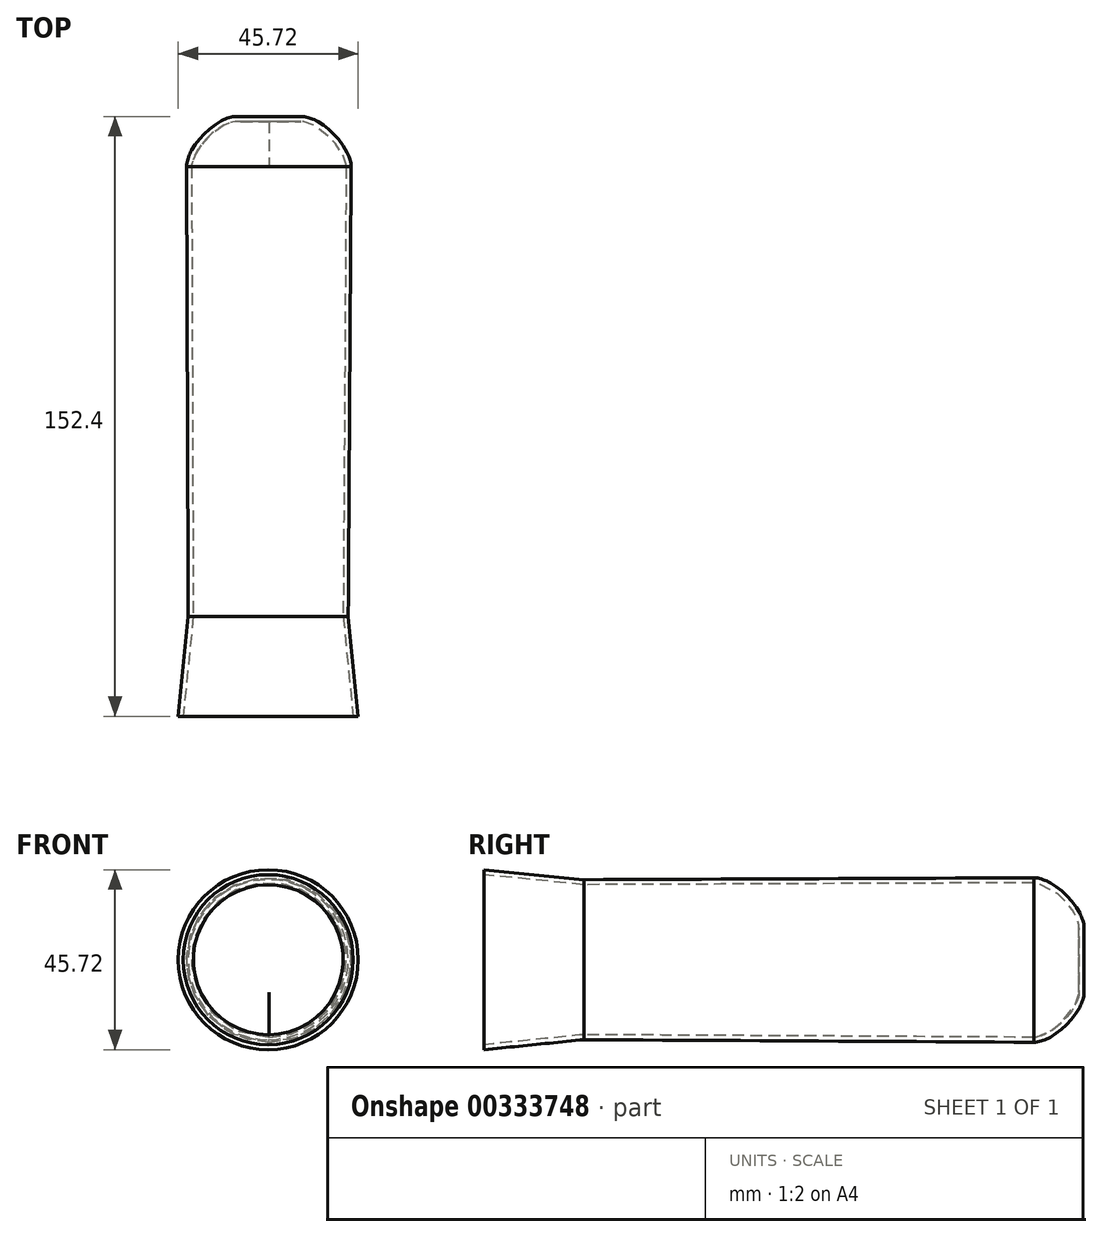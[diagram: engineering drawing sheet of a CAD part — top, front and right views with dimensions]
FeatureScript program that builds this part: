
annotation { "Feature Type Name" : "Feature", "Feature Type Description" : "" }
export const myFeature = defineFeature(function(context is Context, id is Id, definition is map)
    precondition{}
    {
        {
            var Q0;
            Q0=qCreatedBy(makeId("Front.planeOp"),FACE);
            var sketch = newSketch(context, id + "F0", { "sketchPlane" : qUnion([Q0])});
            skCircle(sketch, "E0", {"center": v(0, 0) * mm, "radius": 22.86 * mm});
            skSolve(sketch);
        }
        {
            var Q0;
            Q0=qCreatedBy(makeId("Front.planeOp"),FACE);
            cPlane(context, id + "F1", {"entities" : qUnion([Q0]), "cplaneType" : CPlaneType.OFFSET, "offset" : 25.4 * mm, "oppositeDirection" : true, "width" : 152.4 * mm, "height" : 152.4 * mm});
        }
        {
            var Q0;
            Q0=qCreatedBy(id+"F1.planeOp",FACE);
            var sketch = newSketch(context, id + "F2", { "sketchPlane" : qUnion([Q0])});
            skCircle(sketch, "E1", {"center": v(0, 0) * mm, "radius": 20.32 * mm});
            skSolve(sketch);
        }
        {
            var Q0;
            Q0=qCreatedBy(id+"F1.planeOp",FACE);
            cPlane(context, id + "F3", {"entities" : qUnion([Q0]), "cplaneType" : CPlaneType.OFFSET, "offset" : 127 * mm, "oppositeDirection" : true, "width" : 152.4 * mm, "height" : 152.4 * mm});
        }
        {
            var Q0;
            Q0=qCreatedBy(id+"F3.planeOp",FACE);
            var sketch = newSketch(context, id + "F4", { "sketchPlane" : qUnion([Q0])});
            skCircle(sketch, "E2", {"center": v(0.2, -0.1) * mm, "radius": 20.96 * mm});
            skSolve(sketch);
        }
        {
            var Q0;
            Q0=makeQuery(id+"F0.imprint","IMPRINT",FACE,{"disambiguationData":[TD([[makeQuery(id+"F0.imprint","IMPRINT",EDGE,{"derivedFrom":sQuery(id+"F0.wireOp",EDGE,"E0")}),1.0]])]});
            var Q1;
            Q1=makeQuery(id+"F2.imprint","IMPRINT",FACE,{"disambiguationData":[TD([[makeQuery(id+"F2.imprint","IMPRINT",EDGE,{"derivedFrom":sQuery(id+"F2.wireOp",EDGE,"E1")}),1.0]])]});
            loft(context, id + "F5", {"sheetProfilesArray" : [{ "sheetProfileEntities" : qUnion([Q0]) }, { "sheetProfileEntities" : qUnion([Q1]) }]});
        }
        {
            var Q1;
            Q1=makeQuery(id+"F4.imprint","IMPRINT",FACE,{"disambiguationData":[TD([[makeQuery(id+"F4.imprint","IMPRINT",EDGE,{"derivedFrom":sQuery(id+"F4.wireOp",EDGE,"E2")}),1.0]])]});
            var Q2;
            Q2=makeQuery(id+"F5.opLoft","CAP_FACE",FACE,{"disambiguationData":[OSD([makeQuery(id+"F2.imprint","IMPRINT",FACE,{"disambiguationData":[TD([[makeQuery(id+"F2.imprint","IMPRINT",EDGE,{"derivedFrom":sQuery(id+"F2.wireOp",EDGE,"E1")}),1.0]])]})])],"isStart":true});
            loft(context, id + "F6", {"operationType" : NewBodyOperationType.ADD, "sheetProfilesArray" : [{ "sheetProfileEntities" : qUnion([Q1]) }, { "sheetProfileEntities" : qUnion([Q2]) }]});
        }
        {
            var Q0;
            Q0=makeQuery(id+"F6.opLoft","MID_CAP_EDGE",EDGE,{"disambiguationData":[OSD([sQuery(id+"F4.wireOp",EDGE,"E2")])],"capPos":0.0});
            fillet(context, id + "F7", {"entities" : qUnion([Q0]), "radius" : 12.7 * mm, "tangentPropagation" : true, "rho" : .3, "crossSection" : FilletCrossSection.CONIC, "allowEdgeOverflow" : false});
        }
        {
            var Q0;
            Q0=makeQuery(id+"F5.opLoft","CAP_FACE",FACE,{"disambiguationData":[OSD([makeQuery(id+"F0.imprint","IMPRINT",FACE,{"disambiguationData":[TD([[makeQuery(id+"F0.imprint","IMPRINT",EDGE,{"derivedFrom":sQuery(id+"F0.wireOp",EDGE,"E0")}),1.0]])]})])],"isStart":true});
            shell(context, id + "F8", {"entities" : qUnion([Q0]), "thickness" : 1.27 * mm});
        }
    });
